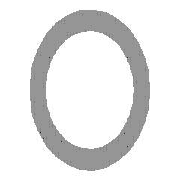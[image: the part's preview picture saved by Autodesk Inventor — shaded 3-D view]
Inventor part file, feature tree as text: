
AUTODESK INVENTOR PART (.ipt)
format: ipt  version: 2021 (Build 250183000, 183)  size: 280,064 bytes
history: native  units: mm (DEFAULTED — no unit token found)
features: other x13, plane x5, sketch x3, sweep x1, extrude x1
ambient origin geometry x8: Origin, YZ Plane, XZ Plane, XY Plane, X Axis, Y Axis, Z Axis, Center Point
bodies: Solid1 (feature_tree)
feature tree (23):
  parser-record x1  (decoder bookkeeping rows leaked as tree rows — omitted from the tree; the rows remain in map.json)
  other  "Driven Length"
  other  "Plano inicial"
  other  "Plano final"
  other  "Trayectoria de barrido"
  plane  "Plano de trabajo de orientación"
  sweep  "Cuerpo"
  plane  "Plano de trabajo5"
  plane  "Plano de trabajo6"
  plane  "Plano de trabajo7"
  extrude  "Extrusión2"  Depth=739.165161mm
  other  "Combinar5"
  sketch  "Sketch3"  dims[d0=33.528mm d1=4.5466mm]
  plane  "Work Plane3"
  sketch  "Sketch4"  dims[d4=-0.0mm d5=739.165161mm]
  sketch  "Boceto5"  dims[d6=90.0deg d7=739.165161mm d8=0.0mm d9=0.0mm d26=0.12mm d27=0.0mm d200=5.0mm d201=0.0mm d202=5.0mm d203=0.0mm]
  other  "Sólido6"
  other  "Sup143"
  other  "Sup144"
  other  "Sólido50"
  other  "Sup142"
  other  "Superficie de contorno95"
  other  "Superficie de contorno96"
